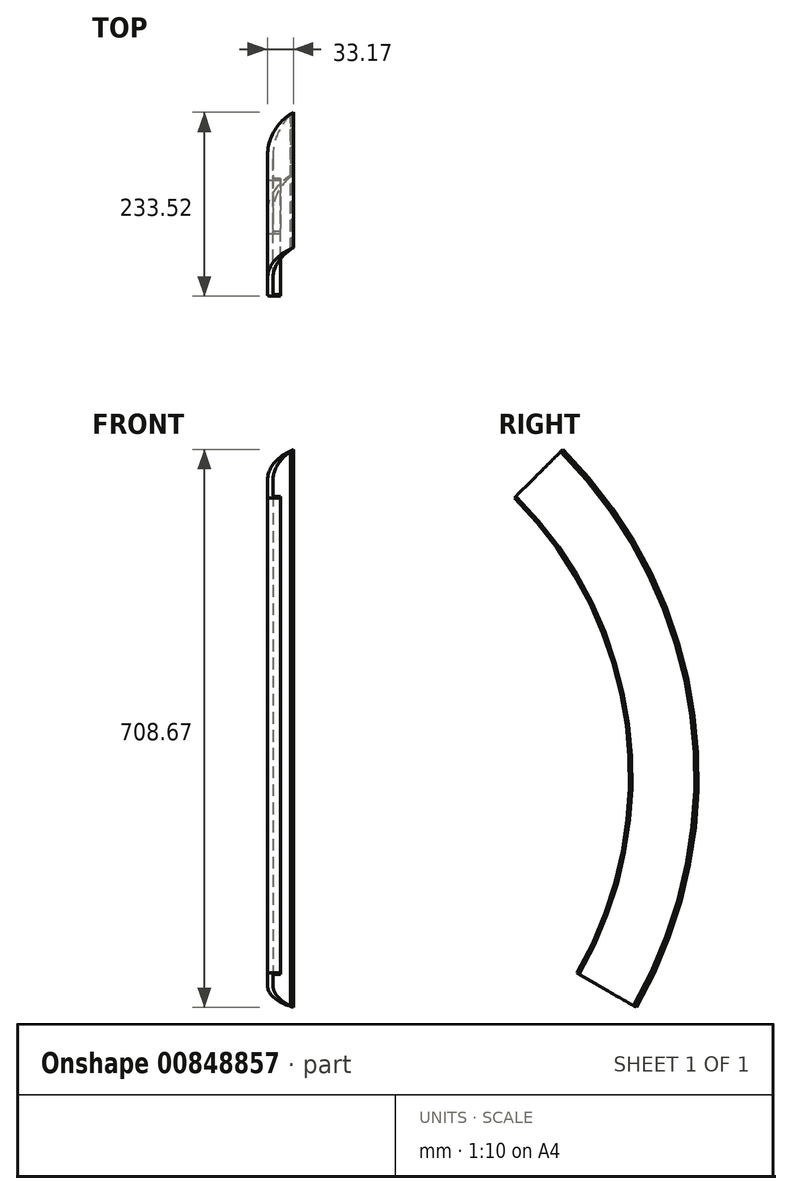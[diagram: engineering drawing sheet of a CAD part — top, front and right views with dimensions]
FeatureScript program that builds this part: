
annotation { "Feature Type Name" : "Feature", "Feature Type Description" : "" }
export const myFeature = defineFeature(function(context is Context, id is Id, definition is map)
    precondition{}
    {
        {
            var Q0;
            Q0=qCreatedBy(makeId("Top.planeOp"),FACE);
            var sketch = newSketch(context, id + "F0", { "sketchPlane" : qUnion([Q0])});
            skLineSegment(sketch, "E0", {"start": v(-8.6, 54.43) * mm, "end": v(-8.6, 24.43) * mm});
            skLineSegment(sketch, "E1", {"start": v(-8.6, 24.43) * mm, "end": v(8.4, 24.43) * mm});
            skLineSegment(sketch, "E2", {"start": v(8.4, 24.43) * mm, "end": v(8.4, 27.43) * mm});
            skLineSegment(sketch, "E3", {"start": v(8.4, 27.43) * mm, "end": v(-1.6, 27.43) * mm});
            skLineSegment(sketch, "E4", {"start": v(-1.6, 27.43) * mm, "end": v(-1.6, 54.43) * mm});
            skArc(sketch, "E5", {"start": v(24.57, 111.5) * mm, "mid": v(0.3, 87.44) * mm, "end": v(-8.6, 54.43) * mm});
            skArc(sketch, "E6", {"start": v(20.65, 107.47) * mm, "mid": v(4.19, 83.19) * mm, "end": v(-1.6, 54.43) * mm});
            skLineSegment(sketch, "E7", {"start": v(24.57, 111.5) * mm, "end": v(20.65, 107.47) * mm});
            skArc(sketch, "E8", {"start": v(22.61, 109.49) * mm, "mid": v(21.64, 109.04) * mm, "end": v(21.22, 108.05) * mm});
            skLineSegment(sketch, "E9", {"start": v(-16.07, -475.57) * mm, "end": v(27.35, -475.57) * mm});
            skSolve(sketch);
        }
        {
            var Q0;
            Q0=makeQuery(id+"F0.imprint","IMPRINT",FACE,{"disambiguationData":[TD([[makeQuery(id+"F0.imprint","IMPRINT",EDGE,{"derivedFrom":sQuery(id+"F0.wireOp",EDGE,"E0")}),1.0]])]});
            var Q1;
            Q1=sQuery(id+"F0.wireOp",EDGE,"E9");
            revolve(context, id + "F1", {"surfaceOperationType" : NewSurfaceOperationType.NEW, "entities" : qUnion([Q0]), "axis" : qUnion([Q1]), "revolveType" : RevolveType.TWO_DIRECTIONS, "angle" : 45 * degree, "angleBack" : 330 * degree});
        }
        {
            var Q0;
            Q0=makeQuery(id+"F1.opRevolve","SWEPT_EDGE",EDGE,{"disambiguationData":[OSD([sQuery(id+"F0.wireOp",EDGE,"E0"),sQuery(id+"F0.wireOp",EDGE,"E1")])]});
            fillet(context, id + "F2", {"entities" : qUnion([Q0]), "radius" : 3 * mm, "tangentPropagation" : true, "allowEdgeOverflow" : false});
        }
        {
            var Q0;
            Q0=makeQuery(id+"F1.opRevolve","SWEPT_EDGE",EDGE,{"disambiguationData":[OSD([sQuery(id+"F0.wireOp",EDGE,"E3"),sQuery(id+"F0.wireOp",EDGE,"E4")])]});
            fillet(context, id + "F3", {"entities" : qUnion([Q0]), "radius" : 3 * mm, "tangentPropagation" : true, "allowEdgeOverflow" : false});
        }
    });
